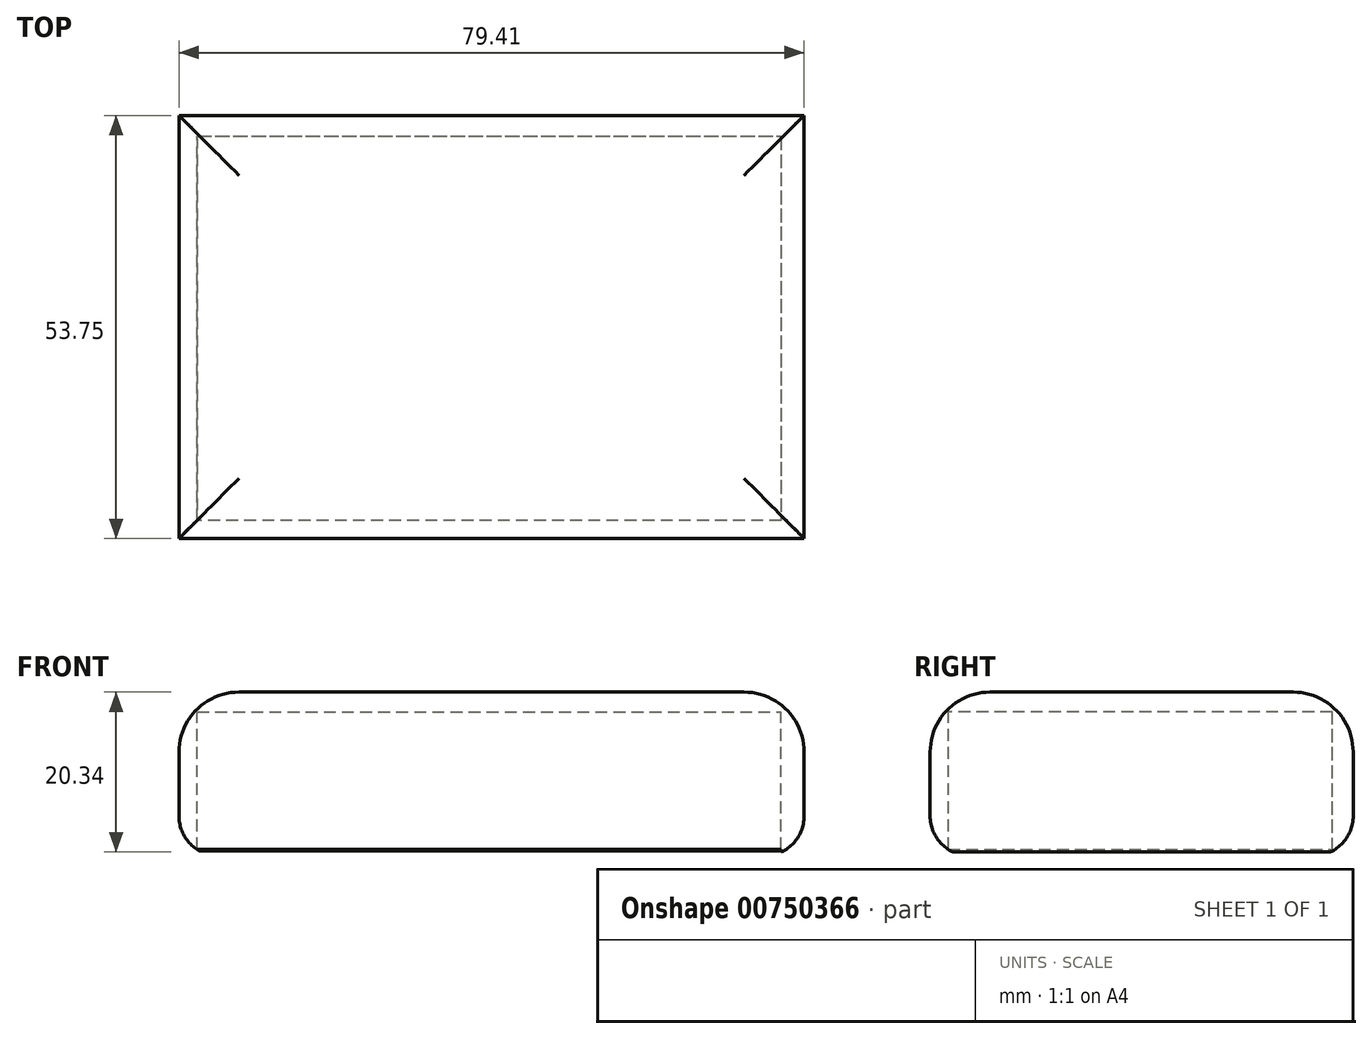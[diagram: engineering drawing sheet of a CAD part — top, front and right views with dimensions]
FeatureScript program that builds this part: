
annotation { "Feature Type Name" : "Feature", "Feature Type Description" : "" }
export const myFeature = defineFeature(function(context is Context, id is Id, definition is map)
    precondition{}
    {
        {
            var Q0;
            Q0=qCreatedBy(makeId("Top.planeOp"),FACE);
            var sketch = newSketch(context, id + "F0", { "sketchPlane" : qUnion([Q0])});
            skLineSegment(sketch, "E0.bottom", {"start": v(-36.27, 27.32) * mm, "end": v(37.93, 27.32) * mm});
            skLineSegment(sketch, "E0.top", {"start": v(-36.27, -21.48) * mm, "end": v(37.93, -21.48) * mm});
            skLineSegment(sketch, "E0.left", {"start": v(-36.27, 27.32) * mm, "end": v(-36.27, -21.48) * mm});
            skLineSegment(sketch, "E0.right", {"start": v(37.93, 27.32) * mm, "end": v(37.93, -21.48) * mm});
            skSolve(sketch);
        }
        {
            var Q0;
            Q0 = qSketchRegion(id + "F0", true);
            extrude(context, id + "F1", {"entities" : qUnion([Q0]), "depth" : 2.54 * mm, "offsetDistance" : 25.4 * mm});
        }
        {
            var Q0;
            Q0=makeQuery(id+"F1.opExtrude","CAP_FACE",FACE,{"disambiguationData":[OSD([sQuery(id+"F0.wireOp",EDGE,"E0.bottom"),sQuery(id+"F0.wireOp",EDGE,"E0.top"),sQuery(id+"F0.wireOp",EDGE,"E0.left"),sQuery(id+"F0.wireOp",EDGE,"E0.right")])],"isStart":false});
            var sketch = newSketch(context, id + "F2", { "sketchPlane" : qUnion([Q0])});
            skLineSegment(sketch, "E1.bottom", {"start": v(-38.57, 29.97) * mm, "end": v(40.84, 29.97) * mm});
            skLineSegment(sketch, "E1.top", {"start": v(-38.57, -23.78) * mm, "end": v(40.84, -23.78) * mm});
            skLineSegment(sketch, "E1.left", {"start": v(-38.57, 29.97) * mm, "end": v(-38.57, -23.78) * mm});
            skLineSegment(sketch, "E1.right", {"start": v(40.84, 29.97) * mm, "end": v(40.84, -23.78) * mm});
            skLineSegment(sketch, "E2.bottom", {"start": v(-36.27, -21.48) * mm, "end": v(37.93, -21.48) * mm});
            skLineSegment(sketch, "E2.top", {"start": v(-36.27, 27.32) * mm, "end": v(37.93, 27.32) * mm});
            skLineSegment(sketch, "E2.left", {"start": v(-36.27, -21.48) * mm, "end": v(-36.27, 27.32) * mm});
            skLineSegment(sketch, "E2.right", {"start": v(37.93, -21.48) * mm, "end": v(37.93, 27.32) * mm});
            skSolve(sketch);
        }
        {
            var Q0;
            Q0 = qSketchRegion(id + "F2", true);
            extrude(context, id + "F3", {"entities" : qUnion([Q0]), "operationType" : NewBodyOperationType.ADD, "oppositeDirection" : true, "depth" : 20.83 * mm, "offsetDistance" : 25.4 * mm});
        }
        {
            var Q0;
            Q0=makeQuery(id+"F3.opExtrude","CAP_EDGE",EDGE,{"disambiguationData":[OSD([sQuery(id+"F2.wireOp",EDGE,"E1.bottom")])],"isStart":true});
            var Q1;
            Q1=makeQuery(id+"F3.opExtrude","CAP_EDGE",EDGE,{"disambiguationData":[OSD([sQuery(id+"F2.wireOp",EDGE,"E1.left")])],"isStart":true});
            var Q2;
            Q2=makeQuery(id+"F3.opExtrude","CAP_EDGE",EDGE,{"disambiguationData":[OSD([sQuery(id+"F2.wireOp",EDGE,"E1.right")])],"isStart":true});
            var Q3;
            Q3=makeQuery(id+"F3.opExtrude","CAP_EDGE",EDGE,{"disambiguationData":[OSD([sQuery(id+"F2.wireOp",EDGE,"E1.top")])],"isStart":true});
            fillet(context, id + "F4", {"entities" : qUnion([Q0, Q1, Q2, Q3]), "radius" : 7.62 * mm, "tangentPropagation" : true, "allowEdgeOverflow" : false});
        }
        {
            var Q0;
            Q0=makeQuery(id+"F3.opExtrude","CAP_EDGE",EDGE,{"disambiguationData":[OSD([sQuery(id+"F2.wireOp",EDGE,"E1.right")])],"isStart":false});
            var Q1;
            Q1=makeQuery(id+"F3.opExtrude","CAP_EDGE",EDGE,{"disambiguationData":[OSD([sQuery(id+"F2.wireOp",EDGE,"E1.top")])],"isStart":false});
            var Q2;
            Q2=makeQuery(id+"F3.opExtrude","CAP_EDGE",EDGE,{"disambiguationData":[OSD([sQuery(id+"F2.wireOp",EDGE,"E1.left")])],"isStart":false});
            var Q3;
            Q3=makeQuery(id+"F3.opExtrude","CAP_EDGE",EDGE,{"disambiguationData":[OSD([sQuery(id+"F2.wireOp",EDGE,"E1.bottom")])],"isStart":false});
            fillet(context, id + "F5", {"entities" : qUnion([Q0, Q1, Q2, Q3]), "radius" : 5.08 * mm, "tangentPropagation" : true, "allowEdgeOverflow" : false});
        }
    });
